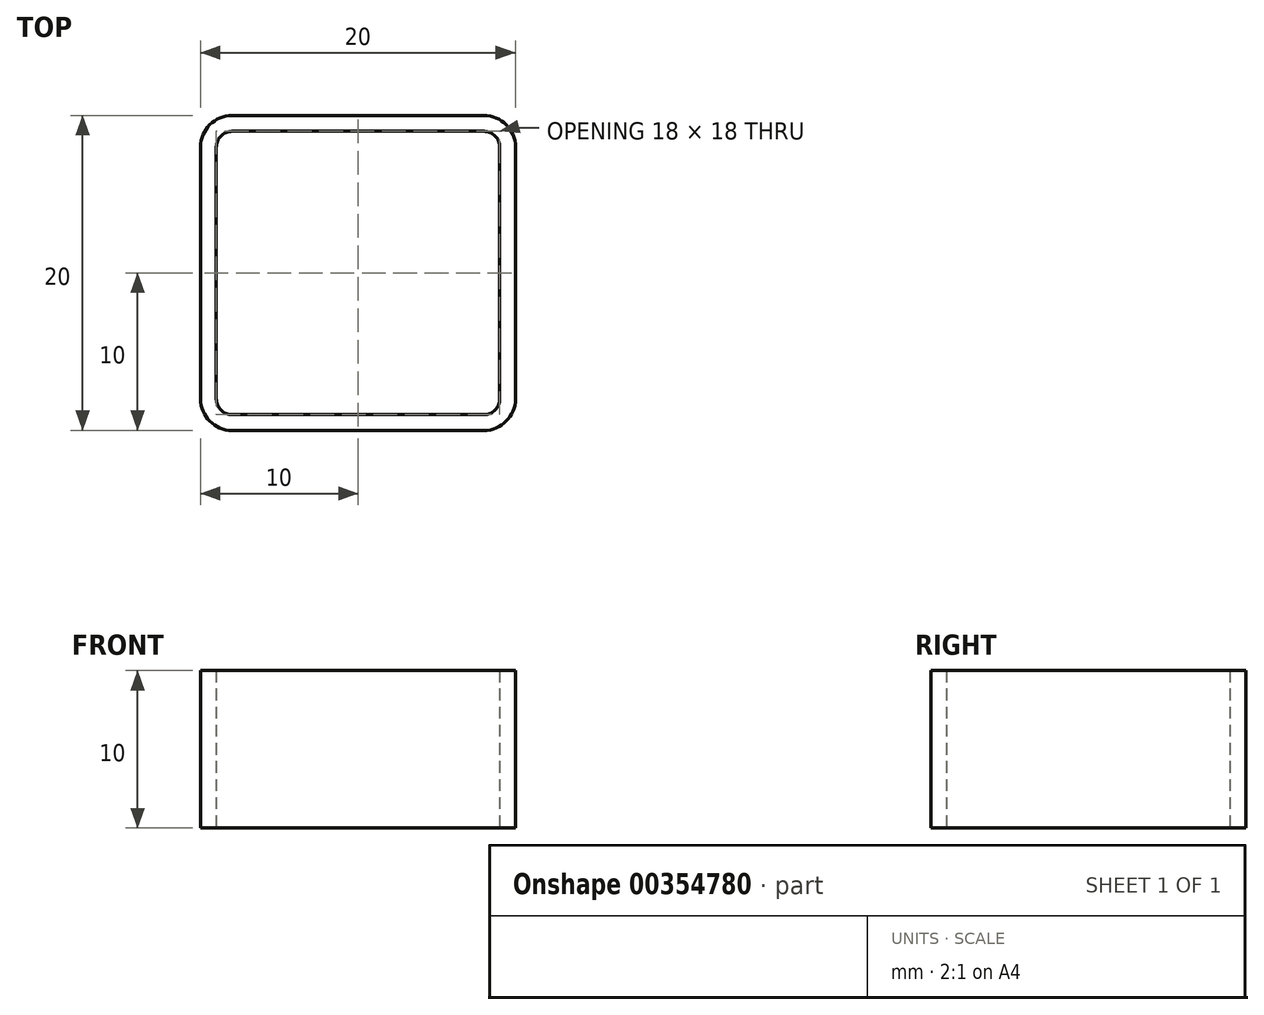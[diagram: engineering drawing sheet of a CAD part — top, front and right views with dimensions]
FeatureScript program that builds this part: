
annotation { "Feature Type Name" : "Feature", "Feature Type Description" : "" }
export const myFeature = defineFeature(function(context is Context, id is Id, definition is map)
    precondition{}
    {
        {
            var Q0;
            Q0=qCreatedBy(makeId("Top.planeOp"),FACE);
            var sketch = newSketch(context, id + "F0", { "sketchPlane" : qUnion([Q0])});
            skLineSegment(sketch, "E0.bottom", {"start": v(2, 0) * mm, "end": v(18, 0) * mm});
            skLineSegment(sketch, "E0.top", {"start": v(2, 20) * mm, "end": v(18, 20) * mm});
            skLineSegment(sketch, "E0.left", {"start": v(0, 2) * mm, "end": v(0, 18) * mm});
            skLineSegment(sketch, "E0.right", {"start": v(20, 2) * mm, "end": v(20, 18) * mm});
            skPoint(sketch, "E1.visualSharp", {"position": v(0, 20) * mm});
            skArc(sketch, "E1.filletArc", {"start": v(2, 20) * mm, "mid": v(0.59, 19.41) * mm, "end": v(0, 18) * mm});
            skPoint(sketch, "E2.visualSharp", {"position": v(20, 20) * mm});
            skArc(sketch, "E2.filletArc", {"start": v(20, 18) * mm, "mid": v(19.41, 19.41) * mm, "end": v(18, 20) * mm});
            skPoint(sketch, "E3.visualSharp", {"position": v(20, 0) * mm});
            skArc(sketch, "E3.filletArc", {"start": v(18, 0) * mm, "mid": v(19.41, 0.59) * mm, "end": v(20, 2) * mm});
            skPoint(sketch, "E4.visualSharp", {"position": v(0, 0) * mm});
            skArc(sketch, "E4.filletArc", {"start": v(0, 2) * mm, "mid": v(0.59, 0.59) * mm, "end": v(2, 0) * mm});
            skLineSegment(sketch, "E5.0", {"start": v(1, 2) * mm, "end": v(1, 18) * mm});
            skLineSegment(sketch, "E5.1", {"start": v(2, 1) * mm, "end": v(18, 1) * mm});
            skLineSegment(sketch, "E5.2", {"start": v(19, 2) * mm, "end": v(19, 18) * mm});
            skLineSegment(sketch, "E5.3", {"start": v(2, 19) * mm, "end": v(18, 19) * mm});
            skPoint(sketch, "E6.visualSharp", {"position": v(19, 19) * mm});
            skArc(sketch, "E6.filletArc", {"start": v(19, 18) * mm, "mid": v(18.7, 18.7) * mm, "end": v(18, 19) * mm});
            skPoint(sketch, "E7.visualSharp", {"position": v(19, 1) * mm});
            skArc(sketch, "E7.filletArc", {"start": v(18, 1) * mm, "mid": v(18.7, 1.3) * mm, "end": v(19, 2) * mm});
            skPoint(sketch, "E8.visualSharp", {"position": v(1, 1) * mm});
            skArc(sketch, "E8.filletArc", {"start": v(1, 2) * mm, "mid": v(1.3, 1.3) * mm, "end": v(2, 1) * mm});
            skPoint(sketch, "E9.visualSharp", {"position": v(1, 19) * mm});
            skArc(sketch, "E9.filletArc", {"start": v(2, 19) * mm, "mid": v(1.3, 18.7) * mm, "end": v(1, 18) * mm});
            skSolve(sketch);
        }
        {
            var Q0;
            Q0 = qSketchRegion(id + "F0", true);
            extrude(context, id + "F1", {"entities" : qUnion([Q0]), "depth" : 10 * mm});
        }
    });
